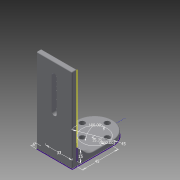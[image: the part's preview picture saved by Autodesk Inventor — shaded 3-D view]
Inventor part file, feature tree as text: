
AUTODESK INVENTOR PART (.ipt)
format: ipt  version: 2013 (Build 170138000, 138)  size: 267,776 bytes
history: native  units: mm
features: extrude x7, sketch x4, fillet x2, hole x1, chamfer x1
ambient origin geometry x8: Origin, YZ Plane, XZ Plane, XY Plane, X Axis, Y Axis, Z Axis, Center Point
bodies: Solid1 (feature_tree)
feature tree (15):
  sketch  "Sketch1"  dims[d0=45.0mm d1=15.75mm]
  extrude  "Extrusion2"  Depth=15.75mm
  extrude  "Extrusion3"  Depth=6.0mm
  hole  "Hole2"  [1 undecoded]
  sketch  "Sketch3"  dims[d2=80.0mm d4=360.0deg d16=6.0mm]
  chamfer  "Chamfer1"  Distance=15.0mm
  extrude  "Extrusion4"  Depth=15.0mm TaperAngle=45.0deg
  fillet  "Fillet1"  Radius=33.0mm
  sketch  "Sketch4"  dims[d17=6.0mm d18=0.0mm d19=106.0mm d20=0.0mm]
  extrude  "Extrusion6"  Depth=15.0mm TaperAngle=0.0deg
  extrude  "Extrusion7"  Depth=14.75mm
  extrude  "Extrusion8"  Depth=45.0mm
  extrude  "Extrusion9"  Depth=0.5mm
  fillet  "Fillet2"  Radius=50.5mm
  sketch  "Sketch5"  dims[d21=6.6mm d22=6.0mm d23=10.4mm d24=2.0mm d25=90.0deg d26=8.0mm d27=20.594885mm d36=15.0mm d37=15.0mm d38=2.0mm d39=45.0deg d40=33.0mm d41=15.0mm d42=0.0mm d43=14.75mm d44=45.0mm d51=0.5mm d52=50.5mm d53=0.5mm d54=10.0mm d55=0.5mm d56=0.5mm d57=0.5mm d58=10.0mm d59=5.0mm d60=5.0mm d61=0.5mm d62=10.0mm d63=0.5mm d64=0.5mm d65=5.0mm d66=5.0mm d69=3.15mm d70=180.0deg d71=3.15mm d72=15.0mm d73=0.0mm d74=0.5mm d75=0.0mm d76=0.5mm d77=0.0mm d78=0.5mm d79=0.0mm d80=1.0mm d81=180.0deg d9=1.0mm d10=1.0mm d82=1.0mm d83=1.0mm]
note: 1 required parameter value undecoded (feature->parameter linkage not recoverable at this tier; creation-order binding heuristic only, values carry confidence <= 0.55)
